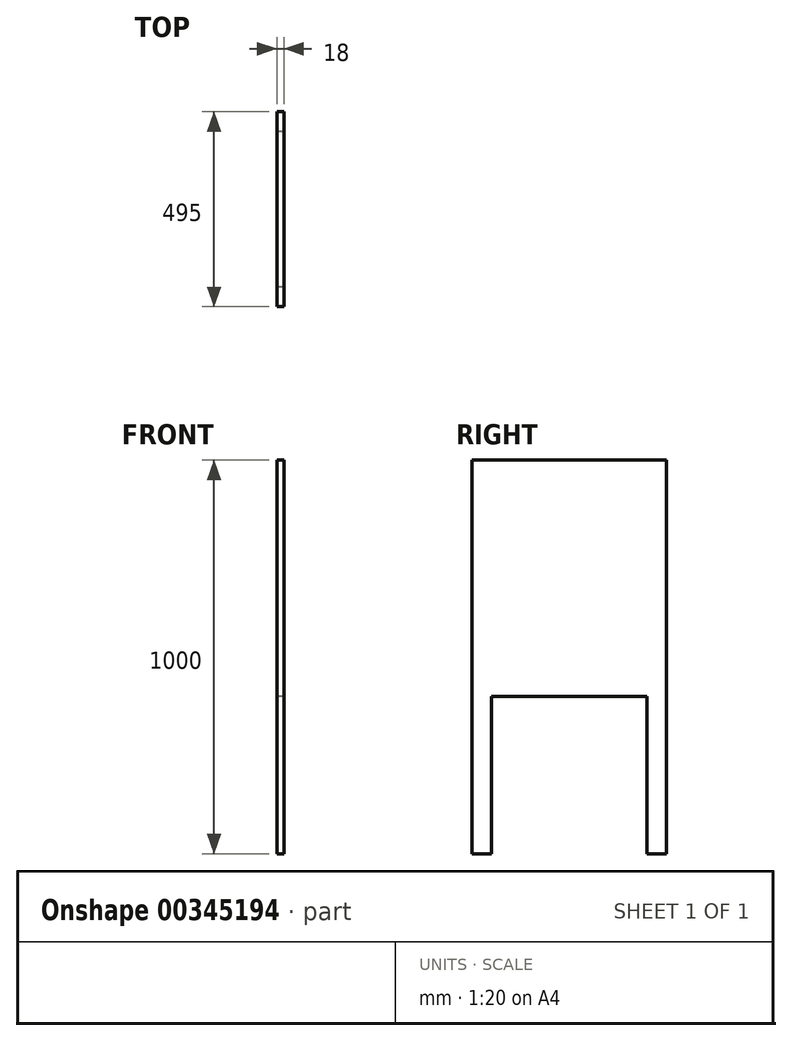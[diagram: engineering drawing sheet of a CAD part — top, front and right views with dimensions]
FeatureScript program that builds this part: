
annotation { "Feature Type Name" : "Feature", "Feature Type Description" : "" }
export const myFeature = defineFeature(function(context is Context, id is Id, definition is map)
    precondition{}
    {
        {
            var Q0;
            Q0=qCreatedBy(makeId("Right.planeOp"),FACE);
            var sketch = newSketch(context, id + "F0", { "sketchPlane" : qUnion([Q0])});
            skLineSegment(sketch, "E0", {"start": v(0, 0) * mm, "end": v(0, 1000) * mm});
            skLineSegment(sketch, "E1", {"start": v(0, 1000) * mm, "end": v(495, 1000) * mm});
            skLineSegment(sketch, "E2", {"start": v(495, 1000) * mm, "end": v(495, 0) * mm});
            skLineSegment(sketch, "E3", {"start": v(495, 0) * mm, "end": v(445, 0) * mm});
            skLineSegment(sketch, "E4", {"start": v(445, 0) * mm, "end": v(445, 400) * mm});
            skLineSegment(sketch, "E5", {"start": v(445, 400) * mm, "end": v(50, 400) * mm});
            skLineSegment(sketch, "E6", {"start": v(50, 400) * mm, "end": v(50, 0) * mm});
            skLineSegment(sketch, "E7", {"start": v(50, 0) * mm, "end": v(0, 0) * mm});
            skSolve(sketch);
        }
        {
            var Q0;
            Q0=makeQuery(id+"F0.imprint","IMPRINT",FACE,{"disambiguationData":[TD([[makeQuery(id+"F0.imprint","IMPRINT",EDGE,{"derivedFrom":sQuery(id+"F0.wireOp",EDGE,"E0")}),-1.0]])]});
            extrude(context, id + "F1", {"entities" : qUnion([Q0]), "depth" : 18 * mm});
        }
    });
